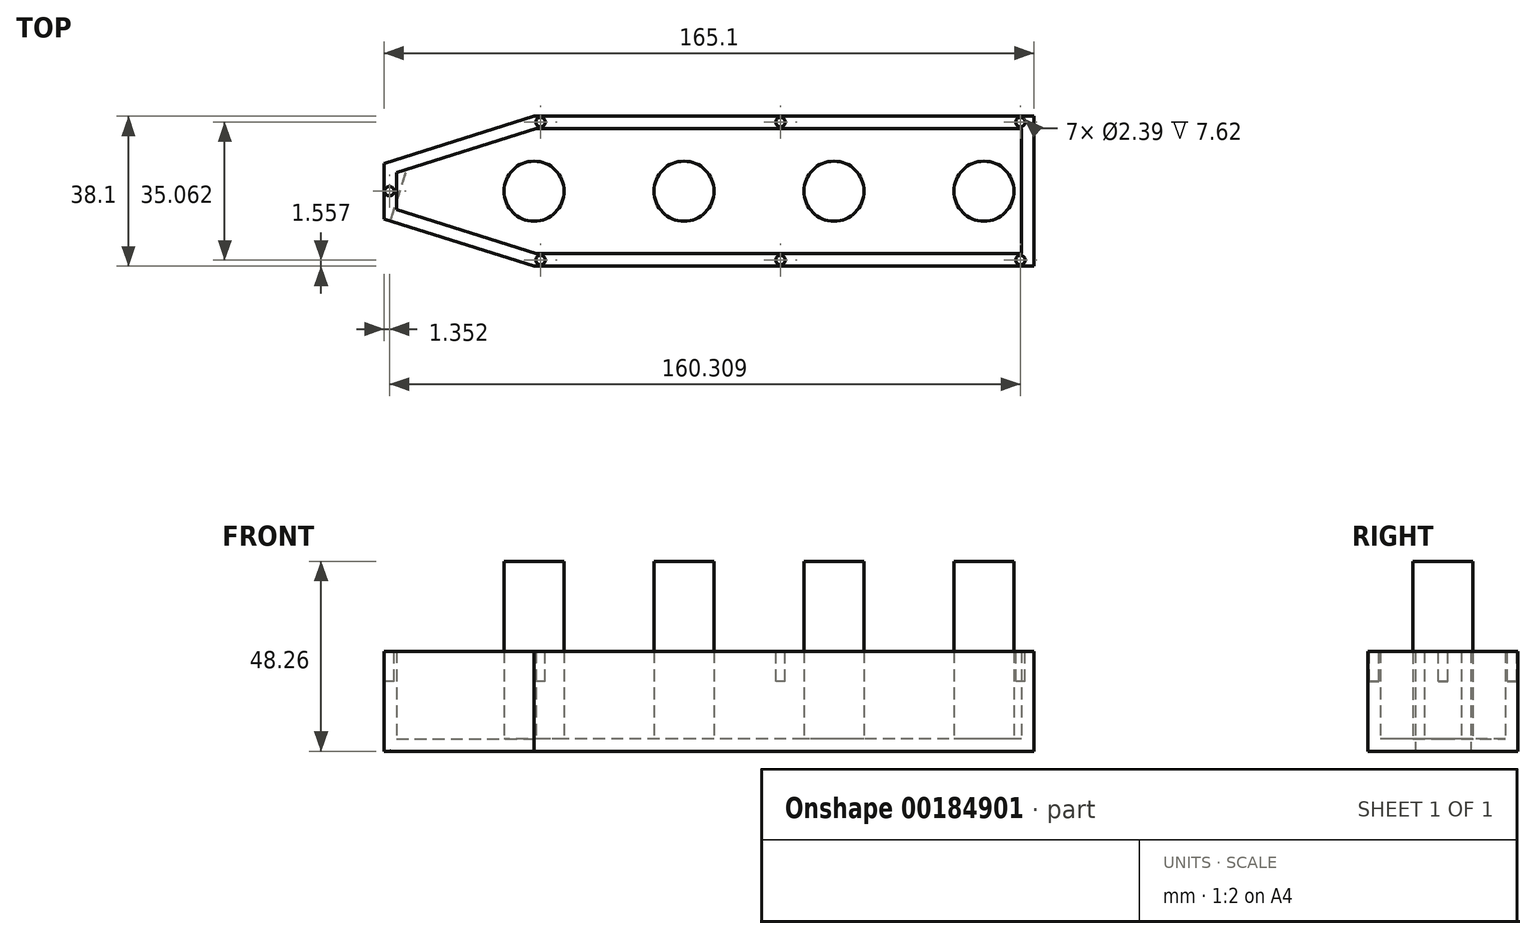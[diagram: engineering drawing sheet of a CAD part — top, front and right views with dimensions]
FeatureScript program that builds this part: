
annotation { "Feature Type Name" : "Feature", "Feature Type Description" : "" }
export const myFeature = defineFeature(function(context is Context, id is Id, definition is map)
    precondition{}
    {
        {
            var Q0;
            Q0=qCreatedBy(makeId("Top.planeOp"),FACE);
            var sketch = newSketch(context, id + "F0", { "sketchPlane" : qUnion([Q0])});
            skLineSegment(sketch, "E0", {"start": v(-38.1, -7.04) * mm, "end": v(0, -19.05) * mm});
            skLineSegment(sketch, "E1", {"start": v(-38.1, 7.04) * mm, "end": v(-38.1, -7.04) * mm});
            skLineSegment(sketch, "E2", {"start": v(-38.1, 7.04) * mm, "end": v(0, 19.05) * mm});
            skLineSegment(sketch, "E3", {"start": v(0, 19.05) * mm, "end": v(127, 19.05) * mm});
            skLineSegment(sketch, "E4", {"start": v(127, 19.05) * mm, "end": v(127, -19.05) * mm});
            skLineSegment(sketch, "E5", {"start": v(127, -19.05) * mm, "end": v(0, -19.05) * mm});
            skPoint(sketch, "E6", {"position": v(-38.1, 0) * mm});
            skSolve(sketch);
        }
        {
            var Q0;
            Q0=makeQuery(id+"F0.imprint","IMPRINT",FACE,{"disambiguationData":[TD([[makeQuery(id+"F0.imprint","IMPRINT",EDGE,{"derivedFrom":sQuery(id+"F0.wireOp",EDGE,"E0")}),1.0]])]});
            extrude(context, id + "F1", {"entities" : qUnion([Q0]), "depth" : 25.4 * mm});
        }
        {
            var Q0;
            Q0=makeQuery(id+"F1.opExtrude","CAP_FACE",FACE,{"disambiguationData":[OSD([sQuery(id+"F0.wireOp",EDGE,"E0"),sQuery(id+"F0.wireOp",EDGE,"E1"),sQuery(id+"F0.wireOp",EDGE,"E2"),sQuery(id+"F0.wireOp",EDGE,"E3"),sQuery(id+"F0.wireOp",EDGE,"E4"),sQuery(id+"F0.wireOp",EDGE,"E5")])],"isStart":false});
            var sketch = newSketch(context, id + "F2", { "sketchPlane" : qUnion([Q0])});
            skCircle(sketch, "E7", {"center": v(0, 0) * mm, "radius": 7.62 * mm});
            skCircle(sketch, "E8.1.0.0", {"center": v(38.1, 0) * mm, "radius": 7.62 * mm});
            skCircle(sketch, "E8.2.0.0", {"center": v(76.2, 0) * mm, "radius": 7.62 * mm});
            skCircle(sketch, "E8.3.0.0", {"center": v(114.3, 0) * mm, "radius": 7.62 * mm});
            skLineSegment(sketch, "E8.direction1", {"start": v(0, 0) * mm, "end": v(38.1, 0) * mm, "construction": true});
            skSolve(sketch);
        }
        {
            var Q0;
            Q0=makeQuery(id+"F1.opExtrude","CAP_FACE",FACE,{"disambiguationData":[OSD([sQuery(id+"F0.wireOp",EDGE,"E0"),sQuery(id+"F0.wireOp",EDGE,"E1"),sQuery(id+"F0.wireOp",EDGE,"E2"),sQuery(id+"F0.wireOp",EDGE,"E3"),sQuery(id+"F0.wireOp",EDGE,"E4"),sQuery(id+"F0.wireOp",EDGE,"E5")])],"isStart":false});
            var Q1;
            Q1=makeQuery(id+"F1.opExtrude","SWEPT_BODY",BODY,{"disambiguationData":[OSD([sQuery(id+"F0.wireOp",EDGE,"E0"),sQuery(id+"F0.wireOp",EDGE,"E1"),sQuery(id+"F0.wireOp",EDGE,"E2"),sQuery(id+"F0.wireOp",EDGE,"E3"),sQuery(id+"F0.wireOp",EDGE,"E4"),sQuery(id+"F0.wireOp",EDGE,"E5")])]});
            shell(context, id + "F3", {"entities" : qUnion([Q0]), "parts" : qUnion([Q1]), "thickness" : 3.17 * mm});
        }
        {
            var Q0;
            Q0=makeQuery(id+"F2.imprint","IMPRINT",FACE,{"disambiguationData":[TD([[makeQuery(id+"F2.imprint","IMPRINT",EDGE,{"derivedFrom":sQuery(id+"F2.wireOp",EDGE,"Y5SaaSIr-AGR2-n8LO-tbhE-mSHLIK7AiV9O")}),1.0]])]});
            var Q1;
            Q1=makeQuery(id+"F2.imprint","IMPRINT",FACE,{"disambiguationData":[TD([[makeQuery(id+"F2.imprint","IMPRINT",EDGE,{"derivedFrom":sQuery(id+"F2.wireOp",EDGE,"ZRmIJm8Z-NGTW-0sMP-mNAe-199w0wXYa2oD")}),1.0]])]});
            var Q2;
            Q2=makeQuery(id+"F2.imprint","IMPRINT",FACE,{"disambiguationData":[TD([[makeQuery(id+"F2.imprint","IMPRINT",EDGE,{"derivedFrom":sQuery(id+"F2.wireOp",EDGE,"8YulFjxc-h3xf-er9p-VXRJ-Hi77Ahz9X9Jc")}),1.0]])]});
            var Q3;
            Q3=makeQuery(id+"F2.imprint","IMPRINT",FACE,{"disambiguationData":[TD([[makeQuery(id+"F2.imprint","IMPRINT",EDGE,{"derivedFrom":sQuery(id+"F2.wireOp",EDGE,"E7")}),1.0]])]});
            var Q4;
            Q4=makeQuery(id+"F2.imprint","IMPRINT",FACE,{"disambiguationData":[TD([[makeQuery(id+"F2.imprint","IMPRINT",EDGE,{"derivedFrom":sQuery(id+"F2.wireOp",EDGE,"E8.1.0.0")}),1.0]])]});
            var Q5;
            Q5=makeQuery(id+"F2.imprint","IMPRINT",FACE,{"disambiguationData":[TD([[makeQuery(id+"F2.imprint","IMPRINT",EDGE,{"derivedFrom":sQuery(id+"F2.wireOp",EDGE,"E8.2.0.0")}),1.0]])]});
            var Q6;
            Q6=makeQuery(id+"F2.imprint","IMPRINT",FACE,{"disambiguationData":[TD([[makeQuery(id+"F2.imprint","IMPRINT",EDGE,{"derivedFrom":sQuery(id+"F2.wireOp",EDGE,"E8.3.0.0")}),1.0]])]});
            var Q7;
            Q7=makeQuery(id+"F3.opShell","OFFSET_FACE",FACE,{"disambiguationData":[OSD([sQuery(id+"F0.wireOp",EDGE,"E0"),sQuery(id+"F0.wireOp",EDGE,"E1"),sQuery(id+"F0.wireOp",EDGE,"E2"),sQuery(id+"F0.wireOp",EDGE,"E3"),sQuery(id+"F0.wireOp",EDGE,"E4"),sQuery(id+"F0.wireOp",EDGE,"E5")])]});
            extrude(context, id + "F4", {"entities" : qUnion([Q0, Q1, Q2, Q3, Q4, Q5, Q6]), "operationType" : NewBodyOperationType.ADD, "depth" : 22.86 * mm, "hasSecondDirection" : true, "secondDirectionBound" : SecondDirectionBoundingType.UP_TO_SURFACE, "secondDirectionOppositeDirection" : true, "secondDirectionBoundEntityFace" : qUnion([Q7]), "secondDirectionDepth" : 25.4 * mm});
        }
        {
            var Q0;
            Q0=makeQuery(id+"F1.opExtrude","CAP_FACE",FACE,{"disambiguationData":[OSD([sQuery(id+"F0.wireOp",EDGE,"E0"),sQuery(id+"F0.wireOp",EDGE,"E1"),sQuery(id+"F0.wireOp",EDGE,"E2"),sQuery(id+"F0.wireOp",EDGE,"E3"),sQuery(id+"F0.wireOp",EDGE,"E4"),sQuery(id+"F0.wireOp",EDGE,"E5")])],"isStart":false});
            var sketch = newSketch(context, id + "F5", { "sketchPlane" : qUnion([Q0])});
            skCircle(sketch, "E9", {"center": v(1.64, 17.57) * mm, "radius": 1.2 * mm});
            skCircle(sketch, "E10.1.0.0", {"center": v(62.6, 17.57) * mm, "radius": 1.2 * mm});
            skCircle(sketch, "E10.2.0.0", {"center": v(123.56, 17.57) * mm, "radius": 1.2 * mm});
            skLineSegment(sketch, "E10.direction1", {"start": v(1.64, 17.57) * mm, "end": v(62.6, 17.57) * mm, "construction": true});
            skCircle(sketch, "E11", {"center": v(-36.75, 0) * mm, "radius": 1.2 * mm});
            skCircle(sketch, "E12", {"center": v(1.64, -17.5) * mm, "radius": 1.2 * mm});
            skCircle(sketch, "E13.1.0.0", {"center": v(62.6, -17.5) * mm, "radius": 1.2 * mm});
            skCircle(sketch, "E13.2.0.0", {"center": v(123.56, -17.5) * mm, "radius": 1.2 * mm});
            skLineSegment(sketch, "E13.direction1", {"start": v(1.64, -17.5) * mm, "end": v(62.6, -17.5) * mm, "construction": true});
            skSolve(sketch);
        }
        {
            var Q0;
            Q0=makeQuery(id+"F5.imprint","IMPRINT",FACE,{"disambiguationData":[TD([[makeQuery(id+"F5.imprint","IMPRINT",EDGE,{"derivedFrom":sQuery(id+"F5.wireOp",EDGE,"E9")}),1.0]])]});
            var Q1;
            Q1=makeQuery(id+"F5.imprint","IMPRINT",FACE,{"disambiguationData":[TD([[makeQuery(id+"F5.imprint","IMPRINT",EDGE,{"derivedFrom":sQuery(id+"F5.wireOp",EDGE,"E10.1.0.0")}),1.0]])]});
            var Q2;
            Q2=makeQuery(id+"F5.imprint","IMPRINT",FACE,{"disambiguationData":[TD([[makeQuery(id+"F5.imprint","IMPRINT",EDGE,{"derivedFrom":sQuery(id+"F5.wireOp",EDGE,"E10.2.0.0")}),1.0]])]});
            var Q3;
            Q3=makeQuery(id+"F5.imprint","IMPRINT",FACE,{"disambiguationData":[TD([[makeQuery(id+"F5.imprint","IMPRINT",EDGE,{"derivedFrom":sQuery(id+"F5.wireOp",EDGE,"E11")}),1.0]])]});
            var Q4;
            Q4=makeQuery(id+"F5.imprint","IMPRINT",FACE,{"disambiguationData":[TD([[makeQuery(id+"F5.imprint","IMPRINT",EDGE,{"derivedFrom":sQuery(id+"F5.wireOp",EDGE,"E13.1.0.0")}),1.0]])]});
            var Q5;
            Q5=makeQuery(id+"F5.imprint","IMPRINT",FACE,{"disambiguationData":[TD([[makeQuery(id+"F5.imprint","IMPRINT",EDGE,{"derivedFrom":sQuery(id+"F5.wireOp",EDGE,"E13.2.0.0")}),1.0]])]});
            var Q6;
            Q6=makeQuery(id+"F5.imprint","IMPRINT",FACE,{"disambiguationData":[TD([[makeQuery(id+"F5.imprint","IMPRINT",EDGE,{"derivedFrom":sQuery(id+"F5.wireOp",EDGE,"E12")}),1.0]])]});
            extrude(context, id + "F6", {"entities" : qUnion([Q0, Q1, Q2, Q3, Q4, Q5, Q6]), "operationType" : NewBodyOperationType.REMOVE, "oppositeDirection" : true, "depth" : 7.62 * mm});
        }
        {
            var Q0;
            Q0=makeQuery(id+"F1.opExtrude","SWEPT_FACE",FACE,{"disambiguationData":[OSD([sQuery(id+"F0.wireOp",EDGE,"E0")])]});
            var sketch = newSketch(context, id + "F7", { "sketchPlane" : qUnion([Q0])});
            skCircle(sketch, "E14", {"center": v(-32.58, 0.09) * mm, "radius": 0.06 * mm});
            skSolve(sketch);
        }
        {
            var Q0;
            Q0=makeQuery(id+"F7.imprint","IMPRINT",FACE,{"disambiguationData":[TD([[makeQuery(id+"F7.imprint","IMPRINT",EDGE,{"derivedFrom":sQuery(id+"F7.wireOp",EDGE,"E14")}),1.0]])]});
            extrude(context, id + "F8", {"entities" : qUnion([Q0]), "operationType" : NewBodyOperationType.REMOVE, "oppositeDirection" : true, "depth" : 12.7 * mm});
        }
    });
